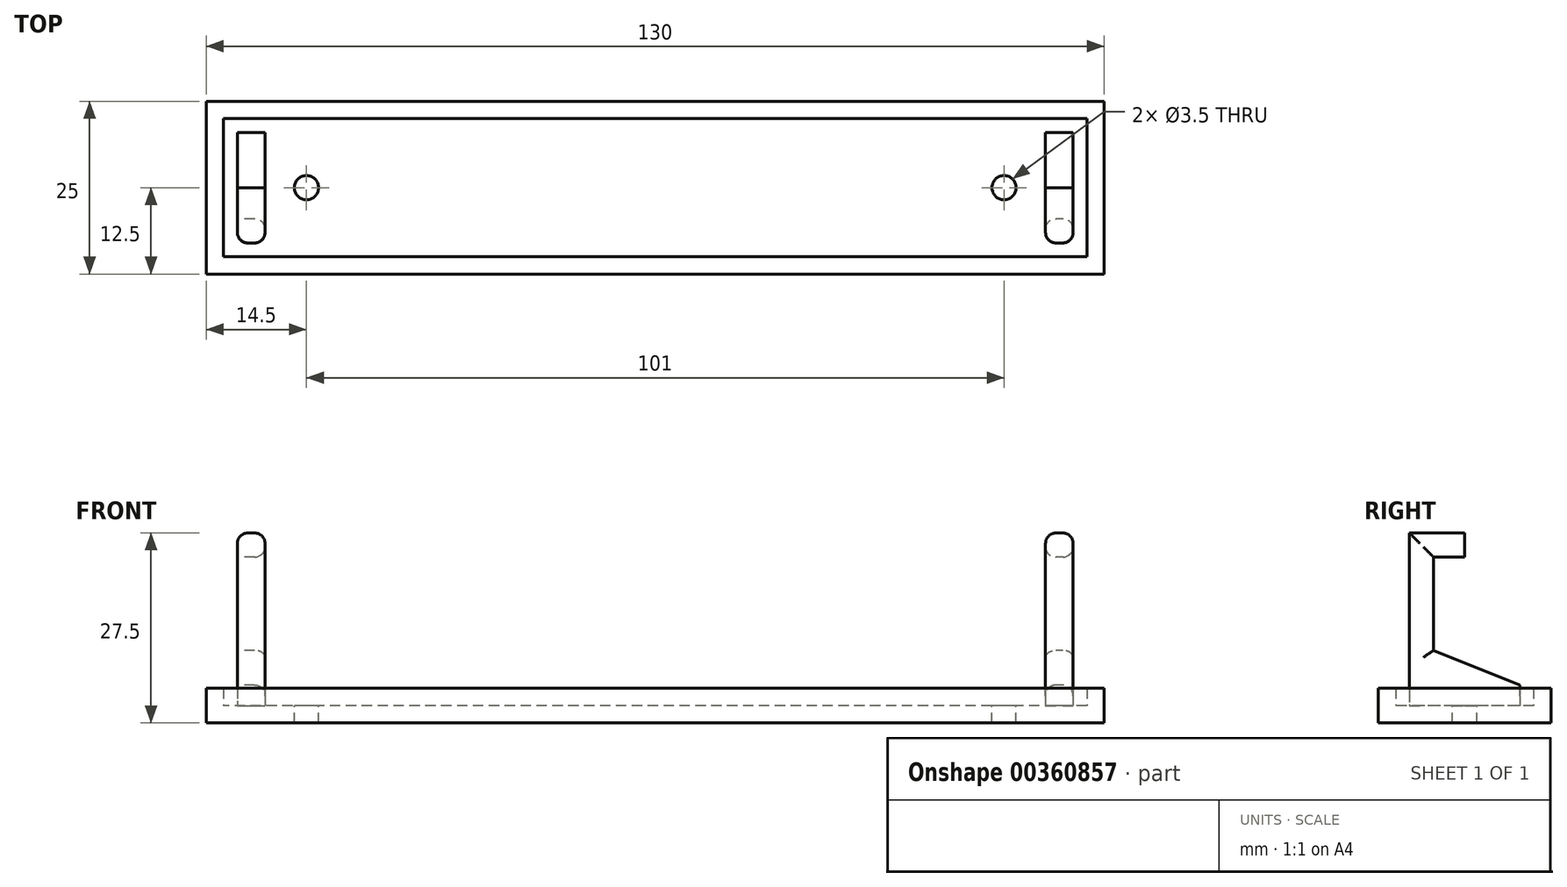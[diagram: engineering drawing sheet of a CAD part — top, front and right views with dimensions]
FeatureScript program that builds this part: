
annotation { "Feature Type Name" : "Feature", "Feature Type Description" : "" }
export const myFeature = defineFeature(function(context is Context, id is Id, definition is map)
    precondition{}
    {
        {
            var Q0;
            Q0=qCreatedBy(makeId("Top.planeOp"),FACE);
            var sketch = newSketch(context, id + "F0", { "sketchPlane" : qUnion([Q0])});
            skLineSegment(sketch, "E0.bottom", {"start": v(65, 12.5) * mm, "end": v(-65, 12.5) * mm});
            skLineSegment(sketch, "E0.top", {"start": v(65, -12.5) * mm, "end": v(-65, -12.5) * mm});
            skLineSegment(sketch, "E0.left", {"start": v(65, 12.5) * mm, "end": v(65, -12.5) * mm});
            skLineSegment(sketch, "E0.right", {"start": v(-65, 12.5) * mm, "end": v(-65, -12.5) * mm});
            skPoint(sketch, "E0.middle", {"position": v(0, 0) * mm});
            skSolve(sketch);
        }
        {
            var Q0;
            Q0 = qSketchRegion(id + "F0", true);
            extrude(context, id + "F1", {"entities" : qUnion([Q0]), "depth" : 5 * mm});
        }
        {
            var Q0;
            Q0=makeQuery(id+"F1.opExtrude","CAP_FACE",FACE,{"disambiguationData":[OSD([sQuery(id+"F0.wireOp",EDGE,"E0.bottom"),sQuery(id+"F0.wireOp",EDGE,"E0.top"),sQuery(id+"F0.wireOp",EDGE,"E0.left"),sQuery(id+"F0.wireOp",EDGE,"E0.right")])],"isStart":false});
            shell(context, id + "F2", {"entities" : qUnion([Q0]), "thickness" : 2.5 * mm});
        }
        {
            var Q0;
            Q0=makeQuery(id+"F2.opShell","OFFSET_FACE",FACE,{"disambiguationData":[OSD([sQuery(id+"F0.wireOp",EDGE,"E0.bottom"),sQuery(id+"F0.wireOp",EDGE,"E0.top"),sQuery(id+"F0.wireOp",EDGE,"E0.left"),sQuery(id+"F0.wireOp",EDGE,"E0.right")])]});
            var sketch = newSketch(context, id + "F3", { "sketchPlane" : qUnion([Q0])});
            skLineSegment(sketch, "E1.bottom", {"start": v(-60.5, 8) * mm, "end": v(-56.5, 8) * mm});
            skLineSegment(sketch, "E1.top", {"start": v(-60.5, -8) * mm, "end": v(-56.5, -8) * mm});
            skLineSegment(sketch, "E1.left", {"start": v(-60.5, 8) * mm, "end": v(-60.5, -8) * mm});
            skLineSegment(sketch, "E1.right", {"start": v(-56.5, 8) * mm, "end": v(-56.5, -8) * mm});
            skLineSegment(sketch, "E2.bottom", {"start": v(60.5, 8) * mm, "end": v(56.5, 8) * mm});
            skLineSegment(sketch, "E2.top", {"start": v(60.5, -8) * mm, "end": v(56.5, -8) * mm});
            skLineSegment(sketch, "E2.left", {"start": v(60.5, 8) * mm, "end": v(60.5, -8) * mm});
            skLineSegment(sketch, "E2.right", {"start": v(56.5, 8) * mm, "end": v(56.5, -8) * mm});
            skSolve(sketch);
        }
        {
            var Q0;
            Q0 = qSketchRegion(id + "F3", true);
            extrude(context, id + "F4", {"entities" : qUnion([Q0]), "operationType" : NewBodyOperationType.ADD, "depth" : 25 * mm});
        }
        {
            var Q0;
            Q0=makeQuery(id+"F4.opExtrude","SWEPT_FACE",FACE,{"disambiguationData":[OSD([sQuery(id+"F3.wireOp",EDGE,"E1.left")])]});
            var sketch = newSketch(context, id + "F5", { "sketchPlane" : qUnion([Q0])});
            skLineSegment(sketch, "E3", {"start": v(0, 27.5) * mm, "end": v(0, 24) * mm});
            skPoint(sketch, "E3.endSnap0", {"position": v(0, 27.5) * mm});
            skLineSegment(sketch, "E4", {"start": v(0, 24) * mm, "end": v(4.5, 24) * mm});
            skLineSegment(sketch, "E5", {"start": v(4.5, 24) * mm, "end": v(4.5, 10.5) * mm});
            skLineSegment(sketch, "E6", {"start": v(4.5, 10.5) * mm, "end": v(-8, 5.5) * mm});
            skLineSegment(sketch, "E7", {"start": v(-8, 5.5) * mm, "end": v(-8, 27.5) * mm});
            skLineSegment(sketch, "E8", {"start": v(-8, 27.5) * mm, "end": v(0, 27.5) * mm});
            skSolve(sketch);
        }
        {
            var Q0;
            Q0 = qSketchRegion(id + "F5", true);
            extrude(context, id + "F6", {"entities" : qUnion([Q0]), "operationType" : NewBodyOperationType.REMOVE, "endBound" : BoundingType.THROUGH_ALL, "oppositeDirection" : true, "depth" : 25 * mm});
        }
        {
            var Q0;
            Q0=makeQuery(id+"F6.boolean.opBoolean","COPY",EDGE,{"derivedFrom":makeQuery(id+"F6.opExtrude","CAP_EDGE",EDGE,{"disambiguationData":[OSD([sQuery(id+"F5.wireOp",EDGE,"E4")])],"isStart":true})});
            var Q1;
            Q1=makeQuery(id+"F4.opExtrude","CAP_EDGE",EDGE,{"disambiguationData":[OSD([sQuery(id+"F3.wireOp",EDGE,"E1.left")])],"isStart":false});
            var Q2;
            Q2=makeQuery(id+"F4.opExtrude","CAP_EDGE",EDGE,{"disambiguationData":[OSD([sQuery(id+"F3.wireOp",EDGE,"E1.right")])],"isStart":false});
            var Q3;
            Q3=makeQuery(id+"F6.boolean.opBoolean","INTERSECT",EDGE,{"derivedFrom":[makeQuery(id+"F4.opExtrude","SWEPT_FACE",FACE,{"disambiguationData":[OSD([sQuery(id+"F3.wireOp",EDGE,"E1.right")])]}),makeQuery(id+"F6.opExtrude","SWEPT_FACE",FACE,{"disambiguationData":[OSD([sQuery(id+"F5.wireOp",EDGE,"E4")])]})]});
            var Q4;
            Q4=makeQuery(id+"F6.boolean.opBoolean","COPY",EDGE,{"derivedFrom":makeQuery(id+"F6.opExtrude","CAP_EDGE",EDGE,{"disambiguationData":[OSD([sQuery(id+"F5.wireOp",EDGE,"E5")])],"isStart":true})});
            var Q5;
            Q5=makeQuery(id+"F6.boolean.opBoolean","INTERSECT",EDGE,{"derivedFrom":[makeQuery(id+"F4.opExtrude","SWEPT_FACE",FACE,{"disambiguationData":[OSD([sQuery(id+"F3.wireOp",EDGE,"E1.right")])]}),makeQuery(id+"F6.opExtrude","SWEPT_FACE",FACE,{"disambiguationData":[OSD([sQuery(id+"F5.wireOp",EDGE,"E5")])]})]});
            var Q6;
            Q6=makeQuery(id+"F4.opExtrude","SWEPT_EDGE",EDGE,{"disambiguationData":[OSD([sQuery(id+"F3.wireOp",EDGE,"E1.top"),sQuery(id+"F3.wireOp",EDGE,"E1.left")])]});
            var Q7;
            Q7=makeQuery(id+"F4.opExtrude","SWEPT_EDGE",EDGE,{"disambiguationData":[OSD([sQuery(id+"F3.wireOp",EDGE,"E1.top"),sQuery(id+"F3.wireOp",EDGE,"E1.right")])]});
            var Q8;
            Q8=makeQuery(id+"F6.boolean.opBoolean","COPY",EDGE,{"derivedFrom":makeQuery(id+"F6.opExtrude","CAP_EDGE",EDGE,{"disambiguationData":[OSD([sQuery(id+"F5.wireOp",EDGE,"E6")])],"isStart":true})});
            var Q9;
            Q9=makeQuery(id+"F6.boolean.opBoolean","INTERSECT",EDGE,{"derivedFrom":[makeQuery(id+"F4.opExtrude","SWEPT_FACE",FACE,{"disambiguationData":[OSD([sQuery(id+"F3.wireOp",EDGE,"E1.right")])]}),makeQuery(id+"F6.opExtrude","SWEPT_FACE",FACE,{"disambiguationData":[OSD([sQuery(id+"F5.wireOp",EDGE,"E6")])]})]});
            fillet(context, id + "F7", {"entities" : qUnion([Q0, Q1, Q2, Q3, Q4, Q5, Q6, Q7, Q8, Q9]), "radius" : 1.5 * mm, "tangentPropagation" : true, "allowEdgeOverflow" : false});
        }
        {
            var Q0;
            Q0=makeQuery(id+"F4.opExtrude","CAP_EDGE",EDGE,{"disambiguationData":[OSD([sQuery(id+"F3.wireOp",EDGE,"E2.left")])],"isStart":false});
            var Q1;
            Q1=makeQuery(id+"F4.opExtrude","CAP_EDGE",EDGE,{"disambiguationData":[OSD([sQuery(id+"F3.wireOp",EDGE,"E2.right")])],"isStart":false});
            var Q2;
            Q2=makeQuery(id+"F6.boolean.opBoolean","INTERSECT",EDGE,{"derivedFrom":[makeQuery(id+"F4.opExtrude","SWEPT_FACE",FACE,{"disambiguationData":[OSD([sQuery(id+"F3.wireOp",EDGE,"E2.left")])]}),makeQuery(id+"F6.opExtrude","SWEPT_FACE",FACE,{"disambiguationData":[OSD([sQuery(id+"F5.wireOp",EDGE,"E4")])]})]});
            var Q3;
            Q3=makeQuery(id+"F6.boolean.opBoolean","INTERSECT",EDGE,{"derivedFrom":[makeQuery(id+"F4.opExtrude","SWEPT_FACE",FACE,{"disambiguationData":[OSD([sQuery(id+"F3.wireOp",EDGE,"E2.left")])]}),makeQuery(id+"F6.opExtrude","SWEPT_FACE",FACE,{"disambiguationData":[OSD([sQuery(id+"F5.wireOp",EDGE,"E5")])]})]});
            var Q4;
            Q4=makeQuery(id+"F4.opExtrude","SWEPT_EDGE",EDGE,{"disambiguationData":[OSD([sQuery(id+"F3.wireOp",EDGE,"E2.top"),sQuery(id+"F3.wireOp",EDGE,"E2.left")])]});
            var Q5;
            Q5=makeQuery(id+"F6.boolean.opBoolean","INTERSECT",EDGE,{"derivedFrom":[makeQuery(id+"F4.opExtrude","SWEPT_FACE",FACE,{"disambiguationData":[OSD([sQuery(id+"F3.wireOp",EDGE,"E2.left")])]}),makeQuery(id+"F6.opExtrude","SWEPT_FACE",FACE,{"disambiguationData":[OSD([sQuery(id+"F5.wireOp",EDGE,"E6")])]})]});
            var Q6;
            Q6=makeQuery(id+"F4.opExtrude","SWEPT_EDGE",EDGE,{"disambiguationData":[OSD([sQuery(id+"F3.wireOp",EDGE,"E2.top"),sQuery(id+"F3.wireOp",EDGE,"E2.right")])]});
            var Q7;
            Q7=makeQuery(id+"F6.boolean.opBoolean","INTERSECT",EDGE,{"derivedFrom":[makeQuery(id+"F4.opExtrude","SWEPT_FACE",FACE,{"disambiguationData":[OSD([sQuery(id+"F3.wireOp",EDGE,"E2.right")])]}),makeQuery(id+"F6.opExtrude","SWEPT_FACE",FACE,{"disambiguationData":[OSD([sQuery(id+"F5.wireOp",EDGE,"E5")])]})]});
            var Q8;
            Q8=makeQuery(id+"F6.boolean.opBoolean","INTERSECT",EDGE,{"derivedFrom":[makeQuery(id+"F4.opExtrude","SWEPT_FACE",FACE,{"disambiguationData":[OSD([sQuery(id+"F3.wireOp",EDGE,"E2.right")])]}),makeQuery(id+"F6.opExtrude","SWEPT_FACE",FACE,{"disambiguationData":[OSD([sQuery(id+"F5.wireOp",EDGE,"E4")])]})]});
            var Q9;
            Q9=makeQuery(id+"F6.boolean.opBoolean","INTERSECT",EDGE,{"derivedFrom":[makeQuery(id+"F4.opExtrude","SWEPT_FACE",FACE,{"disambiguationData":[OSD([sQuery(id+"F3.wireOp",EDGE,"E2.right")])]}),makeQuery(id+"F6.opExtrude","SWEPT_FACE",FACE,{"disambiguationData":[OSD([sQuery(id+"F5.wireOp",EDGE,"E6")])]})]});
            fillet(context, id + "F8", {"entities" : qUnion([Q0, Q1, Q2, Q3, Q4, Q5, Q6, Q7, Q8, Q9]), "radius" : 1.5 * mm, "tangentPropagation" : true, "allowEdgeOverflow" : false});
        }
        {
            var Q0;
            Q0=makeQuery(id+"F2.opShell","OFFSET_FACE",FACE,{"disambiguationData":[OSD([sQuery(id+"F0.wireOp",EDGE,"E0.bottom"),sQuery(id+"F0.wireOp",EDGE,"E0.top"),sQuery(id+"F0.wireOp",EDGE,"E0.left"),sQuery(id+"F0.wireOp",EDGE,"E0.right")])]});
            var sketch = newSketch(context, id + "F9", { "sketchPlane" : qUnion([Q0])});
            skCircle(sketch, "E9", {"center": v(-50.5, 0) * mm, "radius": 1.75 * mm});
            skCircle(sketch, "E10", {"center": v(50.5, 0) * mm, "radius": 1.75 * mm});
            skSolve(sketch);
        }
        {
            var Q0;
            Q0 = qSketchRegion(id + "F9", true);
            extrude(context, id + "F10", {"entities" : qUnion([Q0]), "operationType" : NewBodyOperationType.REMOVE, "endBound" : BoundingType.THROUGH_ALL, "oppositeDirection" : true, "depth" : 25 * mm});
        }
    });
